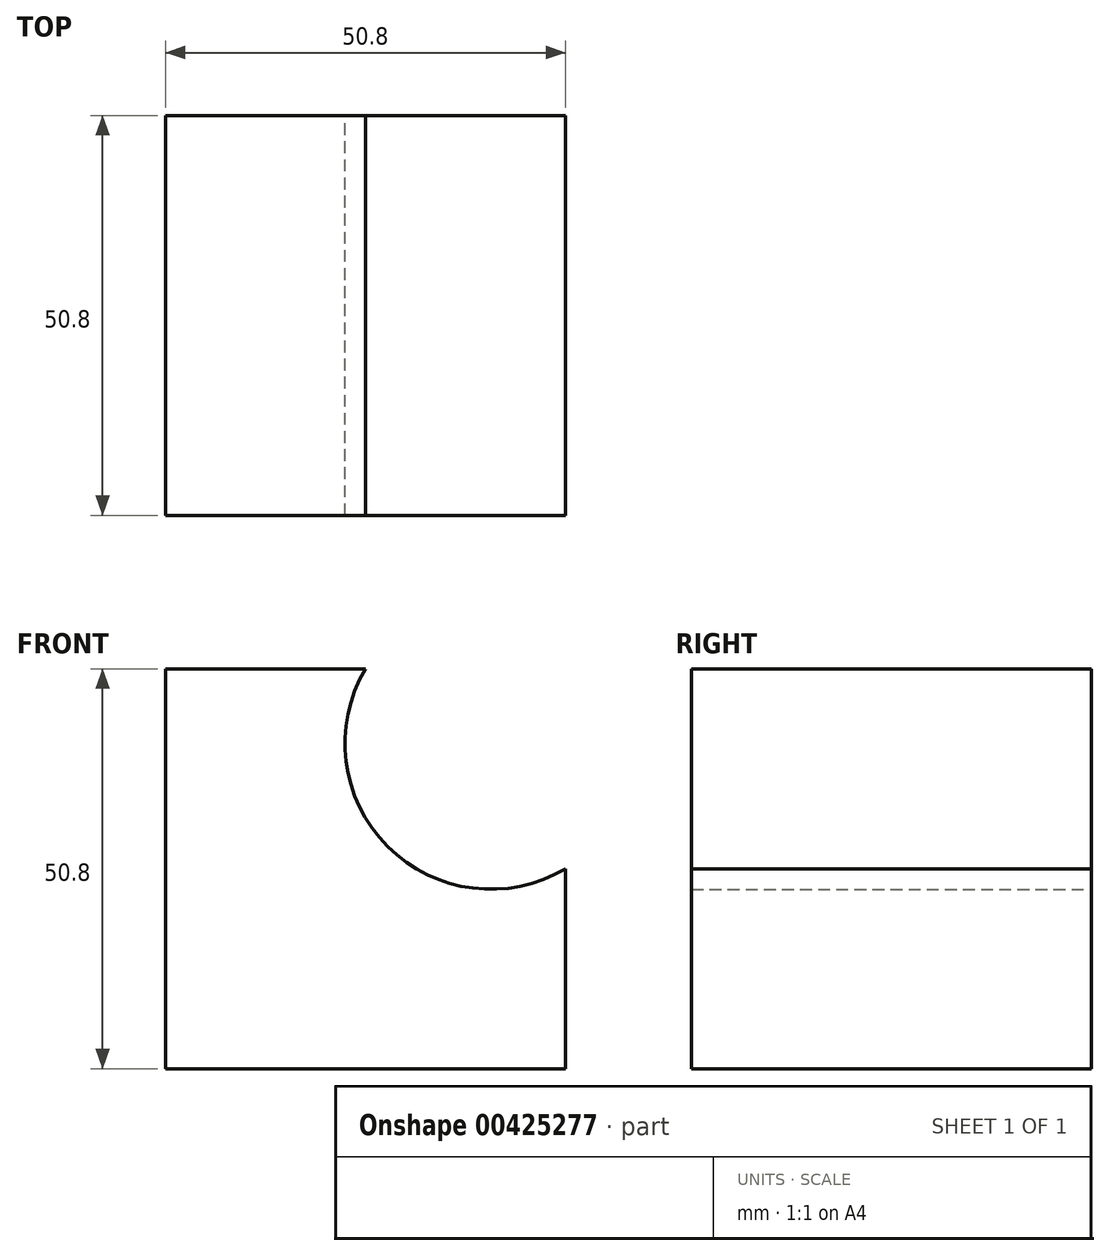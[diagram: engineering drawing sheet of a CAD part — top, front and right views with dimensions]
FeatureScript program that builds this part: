
annotation { "Feature Type Name" : "Feature", "Feature Type Description" : "" }
export const myFeature = defineFeature(function(context is Context, id is Id, definition is map)
    precondition{}
    {
        {
            var Q0;
            Q0=qCreatedBy(makeId("Front.planeOp"),FACE);
            var sketch = newSketch(context, id + "F0", { "sketchPlane" : qUnion([Q0])});
            skLineSegment(sketch, "E0", {"start": v(-50.8, 50.8) * mm, "end": v(-25.4, 50.8) * mm});
            skLineSegment(sketch, "E1", {"start": v(-50.8, 50.8) * mm, "end": v(-50.8, 0) * mm});
            skLineSegment(sketch, "E2", {"start": v(-50.8, 0) * mm, "end": v(0, 0) * mm});
            skLineSegment(sketch, "E3", {"start": v(0, 0) * mm, "end": v(0, 25.4) * mm});
            skArc(sketch, "E4", {"start": v(-25.4, 50.8) * mm, "mid": v(-22.58, 28.22) * mm, "end": v(0, 25.4) * mm});
            skSolve(sketch);
        }
        {
            var Q0;
            Q0 = qSketchRegion(id + "F0", true);
            extrude(context, id + "F1", {"entities" : qUnion([Q0]), "depth" : 50.8 * mm});
        }
    });
